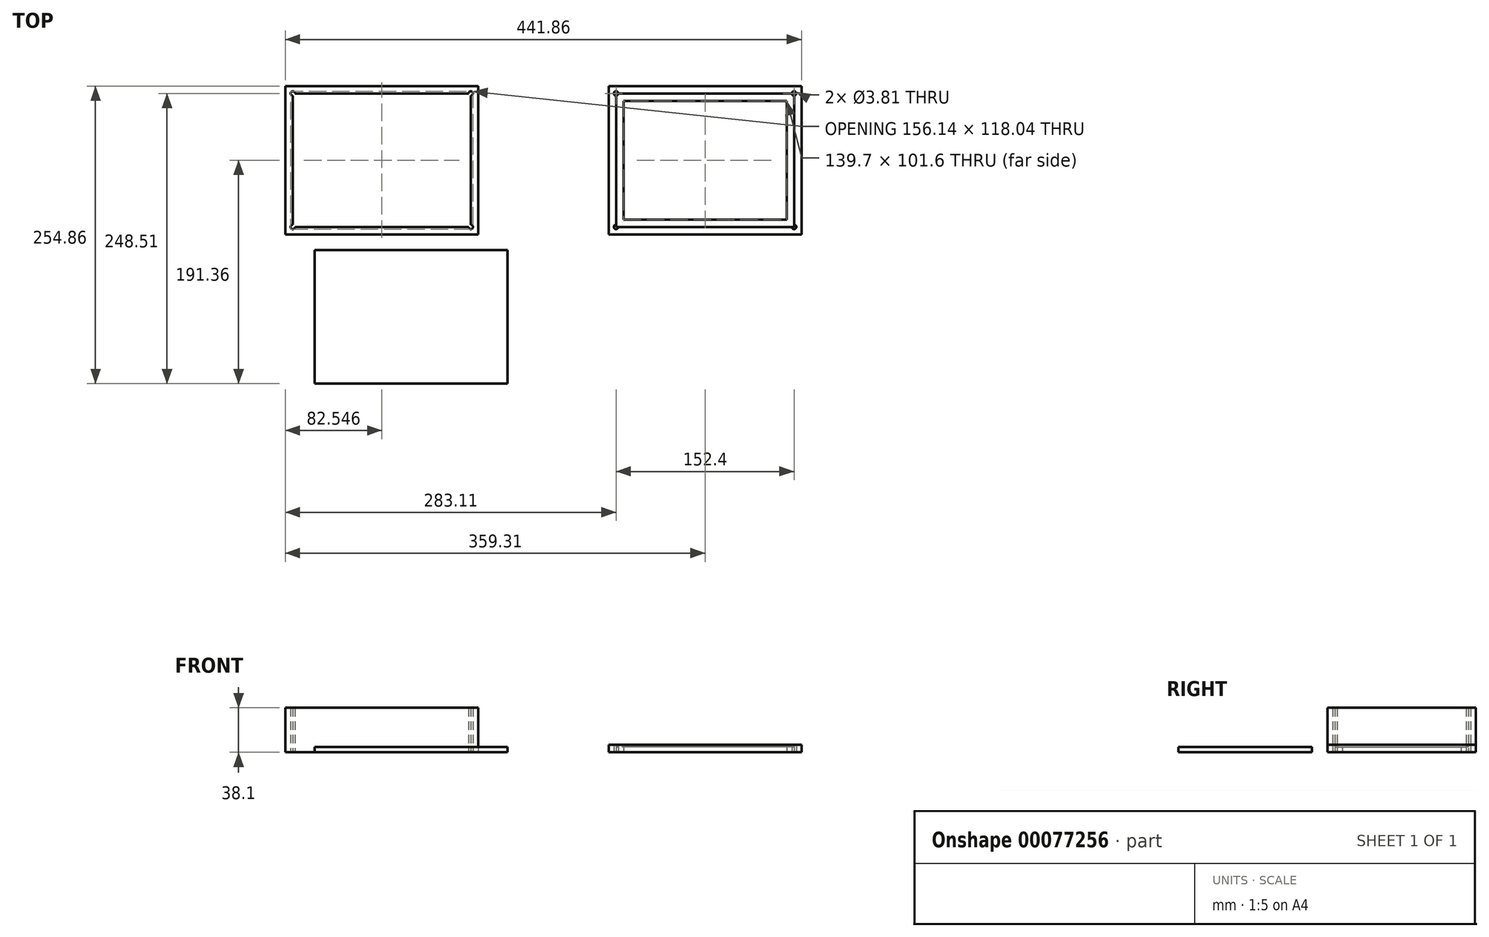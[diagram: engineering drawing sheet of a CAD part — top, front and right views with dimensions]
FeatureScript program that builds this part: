
annotation { "Feature Type Name" : "Feature", "Feature Type Description" : "" }
export const myFeature = defineFeature(function(context is Context, id is Id, definition is map)
    precondition{}
    {
        {
            var Q0;
            Q0=qCreatedBy(makeId("Top.planeOp"),FACE);
            var sketch = newSketch(context, id + "F0", { "sketchPlane" : qUnion([Q0])});
            skLineSegment(sketch, "E0.bottom", {"start": v(82.55, -63.5) * mm, "end": v(-82.55, -63.5) * mm});
            skLineSegment(sketch, "E0.top", {"start": v(82.55, 63.5) * mm, "end": v(-82.55, 63.5) * mm});
            skLineSegment(sketch, "E0.left", {"start": v(82.55, -63.5) * mm, "end": v(82.55, 63.5) * mm});
            skLineSegment(sketch, "E0.right", {"start": v(-82.55, -63.5) * mm, "end": v(-82.55, 63.5) * mm});
            skPoint(sketch, "E0.middle", {"position": v(0, 0) * mm});
            skLineSegment(sketch, "E1.bottom", {"start": v(76.2, -57.15) * mm, "end": v(-76.2, -57.15) * mm});
            skLineSegment(sketch, "E1.top", {"start": v(76.2, 57.15) * mm, "end": v(-76.2, 57.15) * mm});
            skLineSegment(sketch, "E1.left", {"start": v(76.2, -57.15) * mm, "end": v(76.2, 57.15) * mm});
            skLineSegment(sketch, "E1.right", {"start": v(-76.2, -57.15) * mm, "end": v(-76.2, 57.15) * mm});
            skLineSegment(sketch, "E2.bottom", {"start": v(69.85, -50.8) * mm, "end": v(-69.85, -50.8) * mm});
            skLineSegment(sketch, "E2.top", {"start": v(69.85, 50.8) * mm, "end": v(-69.85, 50.8) * mm});
            skLineSegment(sketch, "E2.left", {"start": v(69.85, -50.8) * mm, "end": v(69.85, 50.8) * mm});
            skLineSegment(sketch, "E2.right", {"start": v(-69.85, -50.8) * mm, "end": v(-69.85, 50.8) * mm});
            skCircle(sketch, "E3", {"center": v(-76.2, 57.15) * mm, "radius": 1.9 * mm});
            skCircle(sketch, "E4", {"center": v(76.2, 57.15) * mm, "radius": 1.9 * mm});
            skCircle(sketch, "E5", {"center": v(76.2, -57.15) * mm, "radius": 1.9 * mm});
            skCircle(sketch, "E6", {"center": v(-76.2, -57.15) * mm, "radius": 1.9 * mm});
            skSolve(sketch);
        }
        {
            var Q0;
            Q0=makeQuery(id+"F0.imprint","IMPRINT",FACE,{"disambiguationData":[TD([[makeQuery(id+"F0.imprint","IMPRINT",EDGE,{"derivedFrom":sQuery(id+"F0.wireOp",EDGE,"E1.bottom")}),-1.0]])]});
            var Q1;
            Q1=makeQuery(id+"F0.imprint","IMPRINT",FACE,{"disambiguationData":[TD([[makeQuery(id+"F0.imprint","IMPRINT",EDGE,{"derivedFrom":sQuery(id+"F0.wireOp",EDGE,"E2.bottom")}),1.0]])]});
            extrude(context, id + "F1", {"entities" : qUnion([Q0, Q1]), "depth" : 4.44 * mm});
        }
        {
            var Q0;
            Q0=makeQuery(id+"F0.imprint","IMPRINT",FACE,{"disambiguationData":[TD([[makeQuery(id+"F0.imprint","IMPRINT",EDGE,{"derivedFrom":sQuery(id+"F0.wireOp",EDGE,"E0.bottom")}),-1.0]])]});
            extrude(context, id + "F2", {"entities" : qUnion([Q0]), "operationType" : NewBodyOperationType.ADD, "depth" : 6.35 * mm});
        }
        {
            var Q0;
            Q0=qCreatedBy(makeId("Top.planeOp"),FACE);
            var sketch = newSketch(context, id + "F3", { "sketchPlane" : qUnion([Q0])});
            skLineSegment(sketch, "E7.bottom", {"start": v(-194.21, -63.5) * mm, "end": v(-359.31, -63.5) * mm});
            skLineSegment(sketch, "E7.top", {"start": v(-194.21, 63.5) * mm, "end": v(-359.31, 63.5) * mm});
            skLineSegment(sketch, "E7.left", {"start": v(-194.21, -63.5) * mm, "end": v(-194.21, 63.5) * mm});
            skLineSegment(sketch, "E7.right", {"start": v(-359.31, -63.5) * mm, "end": v(-359.31, 63.5) * mm});
            skPoint(sketch, "E7.middle", {"position": v(-276.76, 0) * mm});
            skLineSegment(sketch, "E8.bottom", {"start": v(-200.56, -57.15) * mm, "end": v(-352.96, -57.15) * mm});
            skLineSegment(sketch, "E8.top", {"start": v(-200.56, 57.15) * mm, "end": v(-352.96, 57.15) * mm});
            skLineSegment(sketch, "E8.left", {"start": v(-200.56, -57.15) * mm, "end": v(-200.56, 57.15) * mm});
            skLineSegment(sketch, "E8.right", {"start": v(-352.96, -57.15) * mm, "end": v(-352.96, 57.15) * mm});
            skCircle(sketch, "E9", {"center": v(-352.96, 57.15) * mm, "radius": 1.9 * mm});
            skCircle(sketch, "E10", {"center": v(-352.96, -57.15) * mm, "radius": 1.9 * mm});
            skCircle(sketch, "E11", {"center": v(-200.56, -57.15) * mm, "radius": 1.9 * mm});
            skCircle(sketch, "E12", {"center": v(-200.56, 57.15) * mm, "radius": 1.9 * mm});
            skSolve(sketch);
        }
        {
            var Q0;
            Q0=makeQuery(id+"F3.imprint","IMPRINT",FACE,{"disambiguationData":[TD([[makeQuery(id+"F3.imprint","IMPRINT",EDGE,{"derivedFrom":sQuery(id+"F3.wireOp",EDGE,"E7.bottom")}),-1.0]])]});
            extrude(context, id + "F4", {"entities" : qUnion([Q0]), "depth" : 38.1 * mm});
        }
        {
            var Q0;
            Q0=qCreatedBy(makeId("Top.planeOp"),FACE);
            var sketch = newSketch(context, id + "F5", { "sketchPlane" : qUnion([Q0])});
            skLineSegment(sketch, "E13.bottom", {"start": v(-169.27, -191.36) * mm, "end": v(-334.37, -191.36) * mm});
            skLineSegment(sketch, "E13.top", {"start": v(-169.27, -77.06) * mm, "end": v(-334.37, -77.06) * mm});
            skLineSegment(sketch, "E13.left", {"start": v(-169.27, -191.36) * mm, "end": v(-169.27, -77.06) * mm});
            skLineSegment(sketch, "E13.right", {"start": v(-334.37, -191.36) * mm, "end": v(-334.37, -77.06) * mm});
            skPoint(sketch, "E13.middle", {"position": v(-251.82, -134.21) * mm});
            skSolve(sketch);
        }
        {
            var Q0;
            Q0=makeQuery(id+"F5.imprint","IMPRINT",FACE,{"disambiguationData":[TD([[makeQuery(id+"F5.imprint","IMPRINT",EDGE,{"derivedFrom":sQuery(id+"F5.wireOp",EDGE,"E13.bottom")}),-1.0]])]});
            extrude(context, id + "F6", {"entities" : qUnion([Q0]), "depth" : 4.44 * mm});
        }
    });
